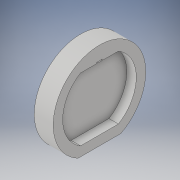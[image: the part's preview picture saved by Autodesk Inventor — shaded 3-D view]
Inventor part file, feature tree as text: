
AUTODESK INVENTOR PART (.ipt)
format: ipt  version: 2017 (Build 210142000, 142)  size: 150,016 bytes
history: native  units: in
note: dims shown in document units (in); Inventor stores cm internally (conversion verified against a paired STEP export)
features: sketch x2, extrude x2, other x1
ambient origin geometry x8: Origin, YZ Plane, XZ Plane, XY Plane, X Axis, Y Axis, Z Axis, Center Point
bodies: Solid3 (feature_tree)
feature tree (5):
  other  "end cap"
  sketch  "Sketch1"  dims[d12=6.6667in d13=4.0in d14=1.0in d15=0.0in d16=1.0in d17=0.0in]
  extrude  "connection"  Depth=1.0in TaperAngle=0.0deg
  extrude  "light\"  Depth=0.0625in
  sketch  "Sketch5"  dims[d18=1.0in d25=0.0625in d32=0.25in d33=0.125in d34=0.0892in d35=0.0884in d36=0.1266in d37=1.0in d38=0.0in]
